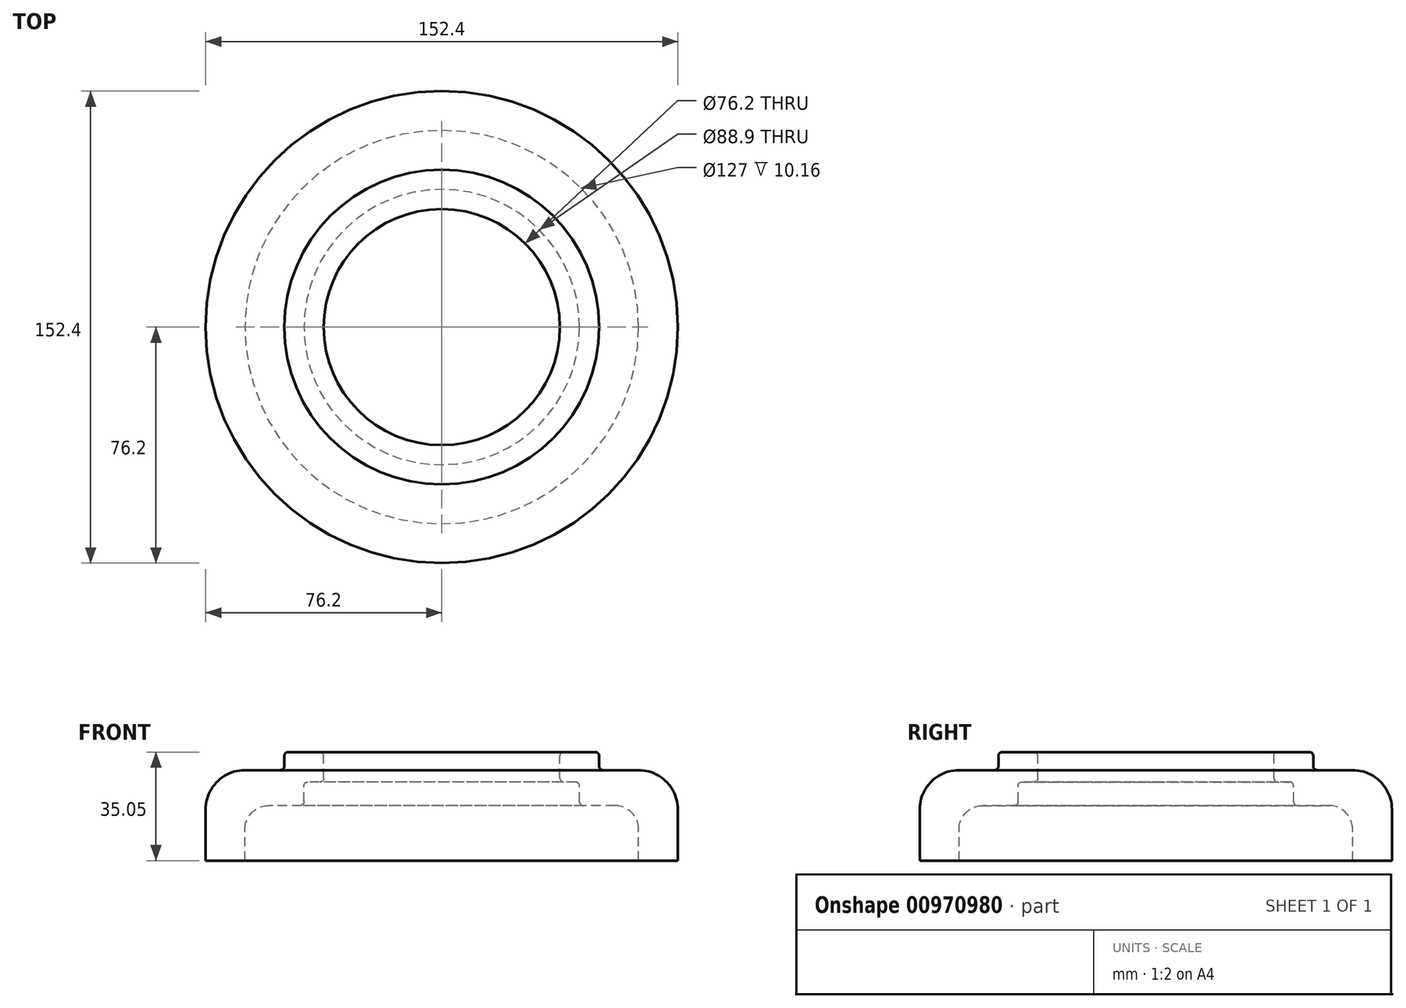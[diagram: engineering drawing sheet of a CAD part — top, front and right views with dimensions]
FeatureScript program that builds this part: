
annotation { "Feature Type Name" : "Feature", "Feature Type Description" : "" }
export const myFeature = defineFeature(function(context is Context, id is Id, definition is map)
    precondition{}
    {
        {
            var Q0;
            Q0=qCreatedBy(makeId("Front.planeOp"),FACE);
            var sketch = newSketch(context, id + "F0", { "sketchPlane" : qUnion([Q0])});
            skLineSegment(sketch, "E0", {"start": v(0, 36.98) * mm, "end": v(0, -52.52) * mm});
            skLineSegment(sketch, "E1", {"start": v(38.1, 1.27) * mm, "end": v(38.1, 8.38) * mm});
            skLineSegment(sketch, "E2", {"start": v(39.37, 9.65) * mm, "end": v(49.53, 9.65) * mm});
            skLineSegment(sketch, "E3", {"start": v(50.8, 8.38) * mm, "end": v(50.8, 5.08) * mm});
            skLineSegment(sketch, "E4", {"start": v(52.07, 3.8) * mm, "end": v(63.5, 3.81) * mm});
            skLineSegment(sketch, "E5", {"start": v(76.2, -8.9) * mm, "end": v(76.2, -25.4) * mm});
            skLineSegment(sketch, "E6", {"start": v(76.2, -25.4) * mm, "end": v(63.5, -25.4) * mm});
            skLineSegment(sketch, "E7", {"start": v(63.5, -25.4) * mm, "end": v(63.5, -15.24) * mm});
            skLineSegment(sketch, "E8", {"start": v(55.88, -7.62) * mm, "end": v(45.72, -7.62) * mm});
            skLineSegment(sketch, "E9", {"start": v(44.45, -6.35) * mm, "end": v(44.45, -1.27) * mm});
            skLineSegment(sketch, "E10", {"start": v(43.18, 0) * mm, "end": v(39.37, 0) * mm});
            skPoint(sketch, "E11.visualSharp", {"position": v(50.8, 3.8) * mm});
            skArc(sketch, "E11.filletArc", {"start": v(50.8, 5.08) * mm, "mid": v(51.17, 4.18) * mm, "end": v(52.07, 3.8) * mm});
            skPoint(sketch, "E12.visualSharp", {"position": v(50.8, 9.65) * mm});
            skArc(sketch, "E12.filletArc", {"start": v(50.8, 8.38) * mm, "mid": v(50.43, 9.28) * mm, "end": v(49.53, 9.65) * mm});
            skPoint(sketch, "E13.visualSharp", {"position": v(38.1, 9.65) * mm});
            skArc(sketch, "E13.filletArc", {"start": v(39.37, 9.65) * mm, "mid": v(38.47, 9.28) * mm, "end": v(38.1, 8.38) * mm});
            skPoint(sketch, "E14.visualSharp", {"position": v(38.1, 0) * mm});
            skArc(sketch, "E14.filletArc", {"start": v(38.1, 1.27) * mm, "mid": v(38.47, 0.37) * mm, "end": v(39.37, 0) * mm});
            skPoint(sketch, "E15.visualSharp", {"position": v(44.45, 0) * mm});
            skArc(sketch, "E15.filletArc", {"start": v(44.45, -1.27) * mm, "mid": v(44.08, -0.37) * mm, "end": v(43.18, 0) * mm});
            skPoint(sketch, "E16.visualSharp", {"position": v(76.2, 3.81) * mm});
            skArc(sketch, "E16.filletArc", {"start": v(76.2, -8.9) * mm, "mid": v(72.48, 0.1) * mm, "end": v(63.5, 3.8) * mm});
            skPoint(sketch, "E17.visualSharp", {"position": v(63.5, -7.62) * mm});
            skArc(sketch, "E17.filletArc", {"start": v(63.5, -15.24) * mm, "mid": v(61.27, -9.85) * mm, "end": v(55.88, -7.62) * mm});
            skPoint(sketch, "E18.visualSharp", {"position": v(44.45, -7.62) * mm});
            skArc(sketch, "E18.filletArc", {"start": v(44.45, -6.35) * mm, "mid": v(44.82, -7.25) * mm, "end": v(45.72, -7.62) * mm});
            skSolve(sketch);
        }
        {
            var Q0;
            Q0 = qSketchRegion(id + "F0", true);
            var Q1;
            Q1=sQuery(id+"F0.wireOp",EDGE,"E0");
            revolve(context, id + "F1", {"surfaceOperationType" : NewSurfaceOperationType.NEW, "entities" : qUnion([Q0]), "axis" : qUnion([Q1]), "revolveType" : RevolveType.FULL});
        }
    });
